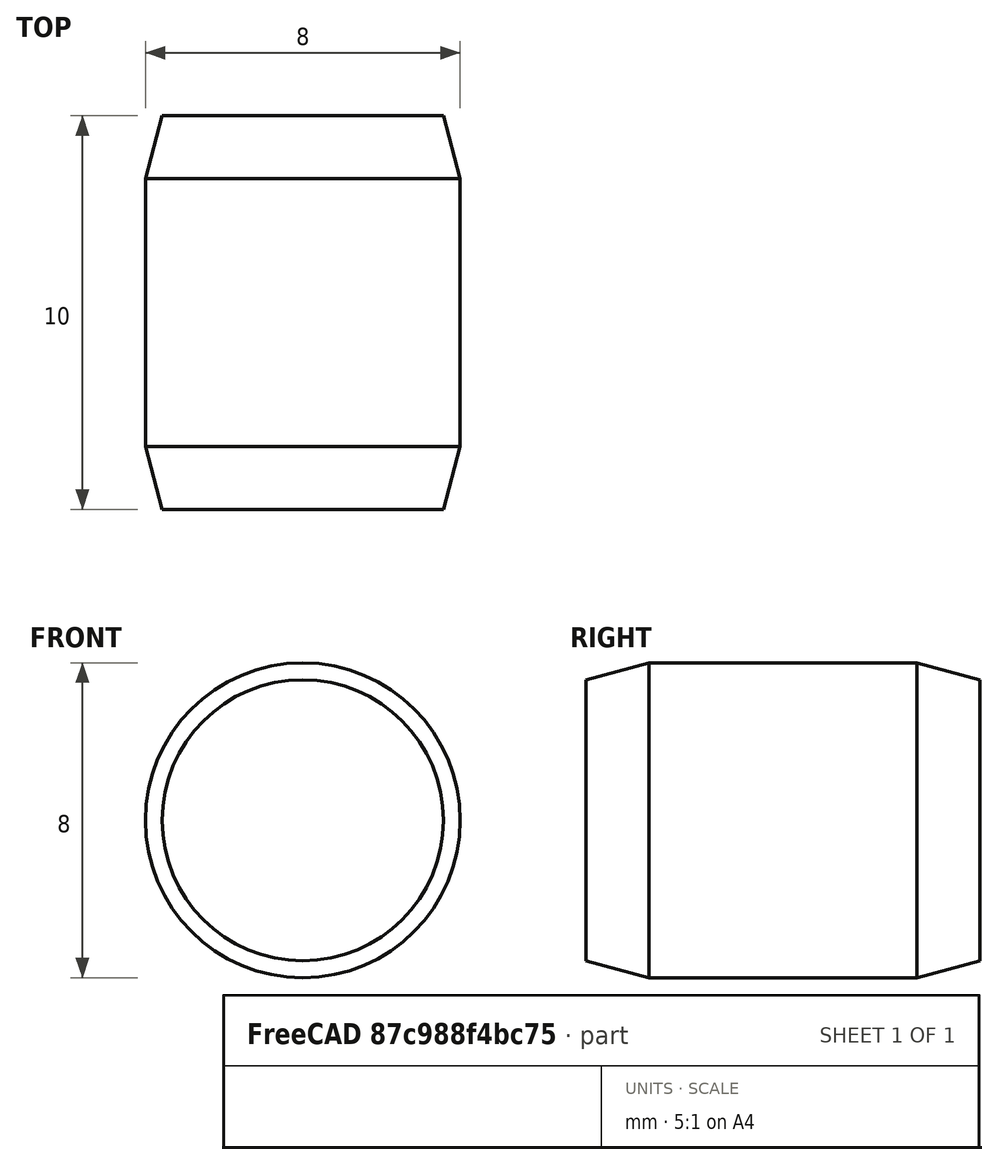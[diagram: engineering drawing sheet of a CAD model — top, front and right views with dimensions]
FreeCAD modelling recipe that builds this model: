
FCSTD DOCUMENT  (FreeCAD 0.15R4470 (Git))
Label: Zyl-Stift_ISO_8734-8x10
License: CC-BY 3.0
LicenseURL: http://creativecommons.org/licenses/by/3.0/
objects: Sketcher::SketchObject×1, PartDesign::Revolution×1
note: 3 computed .brp shape members not serialized (recipe doc carries the construction recipe); baked Part::Feature solids carry a one-line shape summary decoded from their .brp

FEATURE [Sketcher::SketchObject] Sketch
  Placement = pos=(0,0,0) rot=(0.57735,0.57735,0.57735;2.0944rad)
  sketch-geometry (7):
    g0: LineSegment StartX=0 StartY=0 StartZ=0 EndX=0 EndY=3.57128 EndZ=0
    g1: LineSegment StartX=0 StartY=3.57128 StartZ=0 EndX=1.6 EndY=4 EndZ=0
    g2: LineSegment StartX=1.6 StartY=4 StartZ=0 EndX=8.4 EndY=4 EndZ=0
    g3: LineSegment StartX=8.4 StartY=4 StartZ=0 EndX=10 EndY=3.57128 EndZ=0
    g4: LineSegment StartX=10 StartY=3.57128 StartZ=0 EndX=10 EndY=0 EndZ=0
    g5: LineSegment StartX=10 StartY=0 StartZ=0 EndX=0 EndY=0 EndZ=0
    g6: LineSegment [constr] StartX=0 StartY=3.57128 StartZ=0 EndX=10 EndY=3.57128 EndZ=0
  constraints (19):
    c: Coincident(g0,g-1)
    c: PointOnObject(g0,g-2)
    c: Coincident(g0,g1)
    c: Coincident(g1,g2)
    c: Horizontal(g2)
    c: Coincident(g2,g3)
    c: Coincident(g3,g4)
    c: Vertical(g4)
    c: Coincident(g4,g5)
    c: Coincident(g5,g-1)
    c: Horizontal(g5)
    c: Equal(g3,g1)
    c: Coincident(g6,g0)
    c: Coincident(g6,g3)
    c: Horizontal(g6)
    c: Angle(g6,g1) = 0.261799
    c: DistanceY(g-1,g1) = 4
    c: DistanceX(g5) = -10
    c: DistanceX(g1) = 1.6
FEATURE [PartDesign::Revolution] Revolution  label="Zyl-Stift ISO 8734-8x10 #"
  Angle = 360
  Axis = (0,1,0)
  Base = (0,0,0)
  Placement = pos=(0,0,0) rot=(0.57735,0.57735,0.57735;2.0944rad)
  ReferenceAxis = -> Sketch [H_Axis]
  Sketch = -> Sketch
